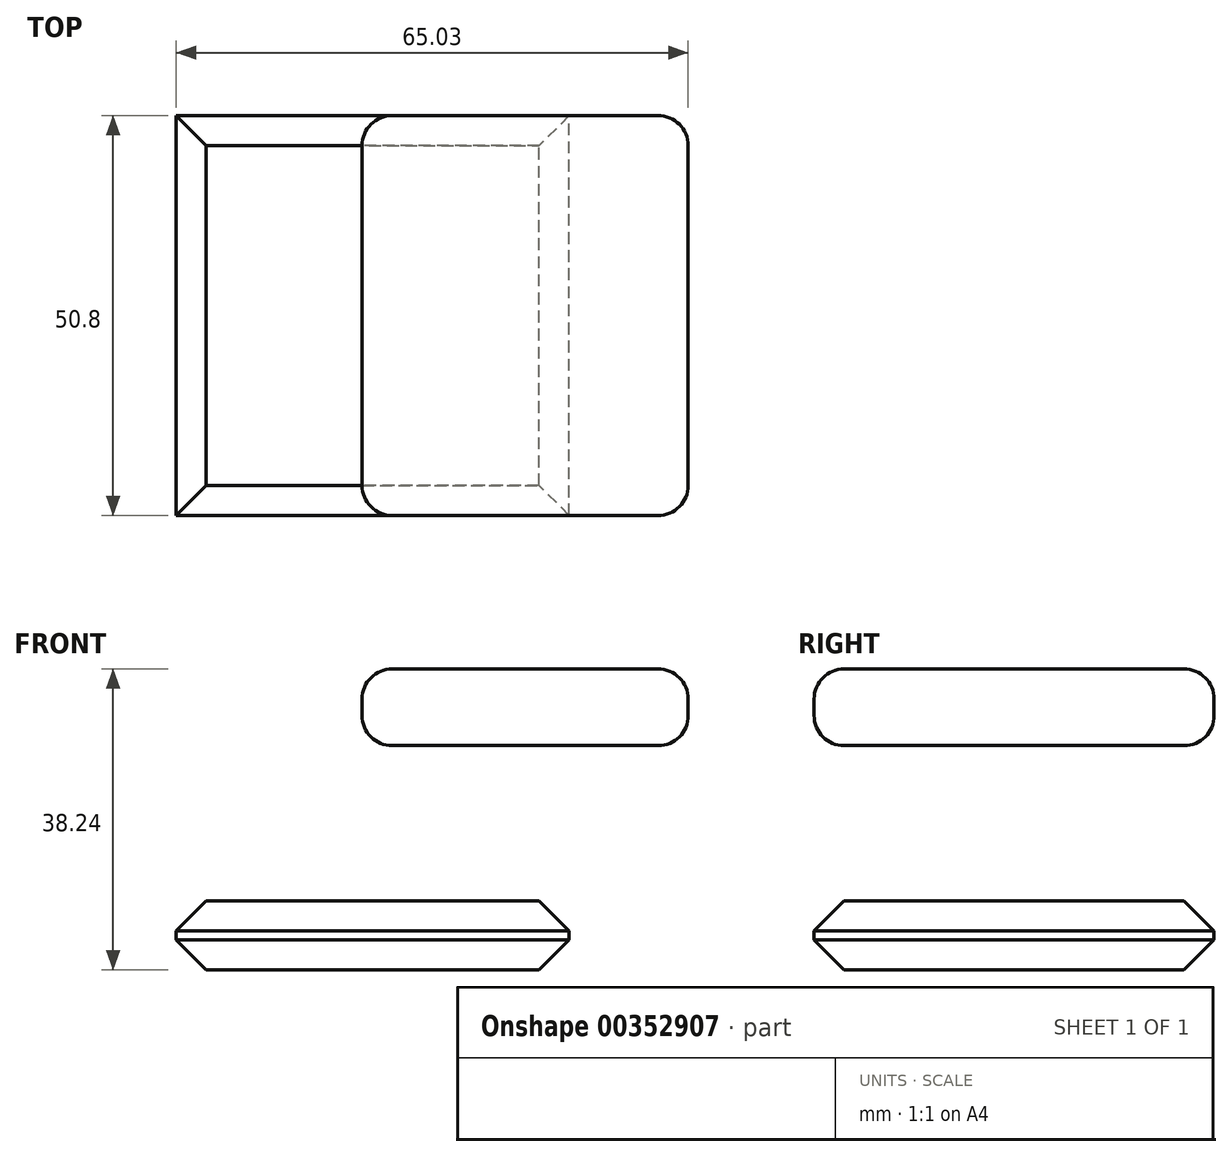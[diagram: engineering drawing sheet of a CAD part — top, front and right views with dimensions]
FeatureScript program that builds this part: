
annotation { "Feature Type Name" : "Feature", "Feature Type Description" : "" }
export const myFeature = defineFeature(function(context is Context, id is Id, definition is map)
    precondition{}
    {
        {
            var Q0;
            Q0=qCreatedBy(makeId("Front.planeOp"),FACE);
            var sketch = newSketch(context, id + "F0", { "sketchPlane" : qUnion([Q0])});
            skLineSegment(sketch, "E0.bottom", {"start": v(-31.42, 21.31) * mm, "end": v(9.99, 21.31) * mm});
            skLineSegment(sketch, "E0.top", {"start": v(-31.42, 11.57) * mm, "end": v(9.99, 11.57) * mm});
            skLineSegment(sketch, "E0.left", {"start": v(-31.42, 21.31) * mm, "end": v(-31.42, 11.57) * mm});
            skLineSegment(sketch, "E0.right", {"start": v(9.99, 21.31) * mm, "end": v(9.99, 11.57) * mm});
            skLineSegment(sketch, "E1.bottom", {"start": v(-55.04, -8.16) * mm, "end": v(-5.11, -8.16) * mm});
            skLineSegment(sketch, "E1.top", {"start": v(-55.04, -16.93) * mm, "end": v(-5.11, -16.93) * mm});
            skLineSegment(sketch, "E1.left", {"start": v(-55.04, -8.16) * mm, "end": v(-55.04, -16.93) * mm});
            skLineSegment(sketch, "E1.right", {"start": v(-5.11, -8.16) * mm, "end": v(-5.11, -16.93) * mm});
            skSolve(sketch);
        }
        {
            var Q0;
            Q0=makeQuery(id+"F0.imprint","IMPRINT",FACE,{"disambiguationData":[TD([[makeQuery(id+"F0.imprint","IMPRINT",EDGE,{"derivedFrom":sQuery(id+"F0.wireOp",EDGE,"E1.bottom")}),-1.0]])]});
            var Q1;
            Q1=makeQuery(id+"F0.imprint","IMPRINT",FACE,{"disambiguationData":[TD([[makeQuery(id+"F0.imprint","IMPRINT",EDGE,{"derivedFrom":sQuery(id+"F0.wireOp",EDGE,"E0.bottom")}),-1.0]])]});
            extrude(context, id + "F1", {"entities" : qUnion([Q0, Q1]), "depth" : 50.8 * mm});
        }
        {
            var Q0;
            Q0=makeQuery(id+"F1.opExtrude","CAP_EDGE",EDGE,{"disambiguationData":[OSD([sQuery(id+"F0.wireOp",EDGE,"E0.bottom")])],"isStart":true});
            var Q1;
            Q1=makeQuery(id+"F1.opExtrude","SWEPT_EDGE",EDGE,{"disambiguationData":[OSD([sQuery(id+"F0.wireOp",EDGE,"E0.bottom"),sQuery(id+"F0.wireOp",EDGE,"E0.right")])]});
            var Q2;
            Q2=makeQuery(id+"F1.opExtrude","CAP_EDGE",EDGE,{"disambiguationData":[OSD([sQuery(id+"F0.wireOp",EDGE,"E0.bottom")])],"isStart":false});
            var Q3;
            Q3=makeQuery(id+"F1.opExtrude","SWEPT_EDGE",EDGE,{"disambiguationData":[OSD([sQuery(id+"F0.wireOp",EDGE,"E0.bottom"),sQuery(id+"F0.wireOp",EDGE,"E0.left")])]});
            var Q4;
            Q4=makeQuery(id+"F1.opExtrude","CAP_EDGE",EDGE,{"disambiguationData":[OSD([sQuery(id+"F0.wireOp",EDGE,"E0.right")])],"isStart":false});
            var Q5;
            Q5=makeQuery(id+"F1.opExtrude","CAP_EDGE",EDGE,{"disambiguationData":[OSD([sQuery(id+"F0.wireOp",EDGE,"E0.left")])],"isStart":false});
            var Q6;
            Q6=makeQuery(id+"F1.opExtrude","CAP_EDGE",EDGE,{"disambiguationData":[OSD([sQuery(id+"F0.wireOp",EDGE,"E0.top")])],"isStart":false});
            var Q7;
            Q7=makeQuery(id+"F1.opExtrude","SWEPT_EDGE",EDGE,{"disambiguationData":[OSD([sQuery(id+"F0.wireOp",EDGE,"E0.top"),sQuery(id+"F0.wireOp",EDGE,"E0.right")])]});
            var Q8;
            Q8=makeQuery(id+"F1.opExtrude","CAP_EDGE",EDGE,{"disambiguationData":[OSD([sQuery(id+"F0.wireOp",EDGE,"E0.right")])],"isStart":true});
            var Q9;
            Q9=makeQuery(id+"F1.opExtrude","CAP_EDGE",EDGE,{"disambiguationData":[OSD([sQuery(id+"F0.wireOp",EDGE,"E0.left")])],"isStart":true});
            var Q10;
            Q10=makeQuery(id+"F1.opExtrude","CAP_EDGE",EDGE,{"disambiguationData":[OSD([sQuery(id+"F0.wireOp",EDGE,"E0.top")])],"isStart":true});
            var Q11;
            Q11=makeQuery(id+"F1.opExtrude","SWEPT_EDGE",EDGE,{"disambiguationData":[OSD([sQuery(id+"F0.wireOp",EDGE,"E0.top"),sQuery(id+"F0.wireOp",EDGE,"E0.left")])]});
            fillet(context, id + "F2", {"entities" : qUnion([Q0, Q1, Q2, Q3, Q4, Q5, Q6, Q7, Q8, Q9, Q10, Q11]), "radius" : 3.8 * mm, "tangentPropagation" : true, "allowEdgeOverflow" : false});
        }
        {
            var Q0;
            Q0=makeQuery(id+"F1.opExtrude","CAP_EDGE",EDGE,{"disambiguationData":[OSD([sQuery(id+"F0.wireOp",EDGE,"E1.bottom")])],"isStart":true});
            var Q1;
            Q1=makeQuery(id+"F1.opExtrude","CAP_EDGE",EDGE,{"disambiguationData":[OSD([sQuery(id+"F0.wireOp",EDGE,"E1.top")])],"isStart":true});
            var Q2;
            Q2=makeQuery(id+"F1.opExtrude","SWEPT_EDGE",EDGE,{"disambiguationData":[OSD([sQuery(id+"F0.wireOp",EDGE,"E1.bottom"),sQuery(id+"F0.wireOp",EDGE,"E1.left")])]});
            var Q3;
            Q3=makeQuery(id+"F1.opExtrude","SWEPT_EDGE",EDGE,{"disambiguationData":[OSD([sQuery(id+"F0.wireOp",EDGE,"E1.top"),sQuery(id+"F0.wireOp",EDGE,"E1.left")])]});
            var Q4;
            Q4=makeQuery(id+"F1.opExtrude","SWEPT_EDGE",EDGE,{"disambiguationData":[OSD([sQuery(id+"F0.wireOp",EDGE,"E1.bottom"),sQuery(id+"F0.wireOp",EDGE,"E1.right")])]});
            var Q5;
            Q5=makeQuery(id+"F1.opExtrude","CAP_EDGE",EDGE,{"disambiguationData":[OSD([sQuery(id+"F0.wireOp",EDGE,"E1.bottom")])],"isStart":false});
            var Q6;
            Q6=makeQuery(id+"F1.opExtrude","CAP_EDGE",EDGE,{"disambiguationData":[OSD([sQuery(id+"F0.wireOp",EDGE,"E1.top")])],"isStart":false});
            var Q7;
            Q7=makeQuery(id+"F1.opExtrude","SWEPT_EDGE",EDGE,{"disambiguationData":[OSD([sQuery(id+"F0.wireOp",EDGE,"E1.top"),sQuery(id+"F0.wireOp",EDGE,"E1.right")])]});
            chamfer(context, id + "F3", {"entities" : qUnion([Q0, Q1, Q2, Q3, Q4, Q5, Q6, Q7]), "width" : 3.8 * mm, "tangentPropagation" : true});
        }
    });
